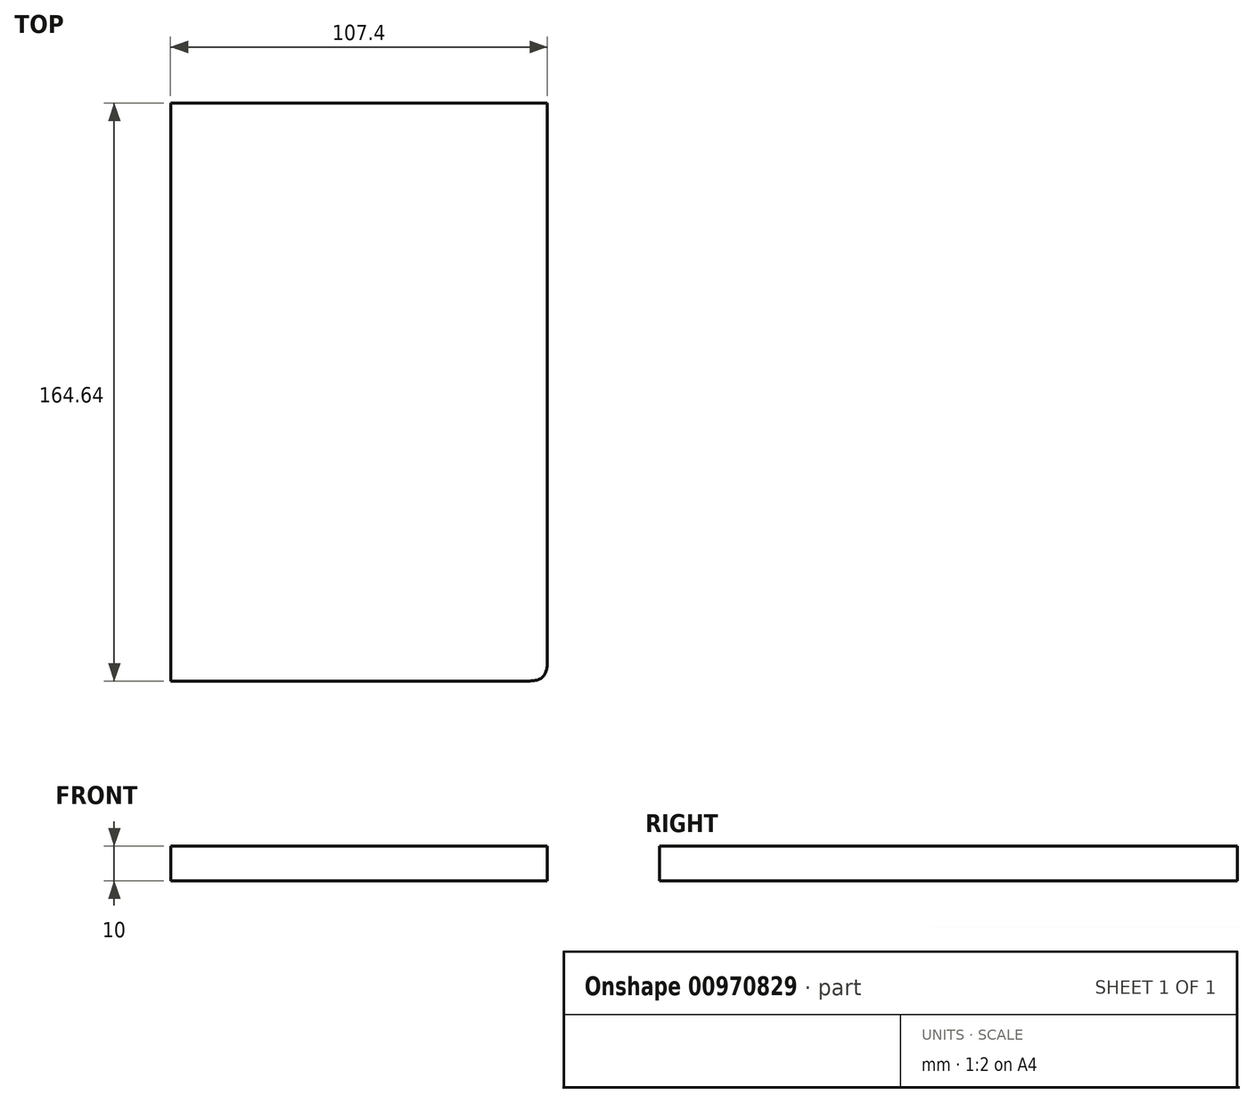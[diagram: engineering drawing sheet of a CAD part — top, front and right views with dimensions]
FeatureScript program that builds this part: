
annotation { "Feature Type Name" : "Feature", "Feature Type Description" : "" }
export const myFeature = defineFeature(function(context is Context, id is Id, definition is map)
    precondition{}
    {
        {
            var Q0;
            Q0=qCreatedBy(makeId("Top.planeOp"),FACE);
            var sketch = newSketch(context, id + "F0", { "sketchPlane" : qUnion([Q0])});
            skLineSegment(sketch, "E0.bottom", {"start": v(53.7, -82.32) * mm, "end": v(-53.7, -82.32) * mm});
            skLineSegment(sketch, "E0.top", {"start": v(53.7, 82.32) * mm, "end": v(-53.7, 82.32) * mm});
            skLineSegment(sketch, "E0.left", {"start": v(53.7, -82.32) * mm, "end": v(53.7, 82.32) * mm});
            skLineSegment(sketch, "E0.right", {"start": v(-53.7, -82.32) * mm, "end": v(-53.7, 82.32) * mm});
            skPoint(sketch, "E0.middle", {"position": v(0, 0) * mm});
            skSolve(sketch);
        }
        {
            var Q0;
            Q0 = qSketchRegion(id + "F0", true);
            extrude(context, id + "F1", {"entities" : qUnion([Q0]), "depth" : 10 * mm, "offsetDistance" : 25 * mm});
        }
        {
            var Q0;
            Q0=makeQuery(id+"F1.opExtrude","SWEPT_EDGE",EDGE,{"disambiguationData":[OSD([sQuery(id+"F0.wireOp",EDGE,"E0.bottom"),sQuery(id+"F0.wireOp",EDGE,"E0.left")])]});
            fillet(context, id + "F2", {"entities" : qUnion([Q0]), "radius" : 5 * mm, "tangentPropagation" : true, "rho" : 0.5, "crossSection" : FilletCrossSection.CONIC, "allowEdgeOverflow" : false});
        }
    });
